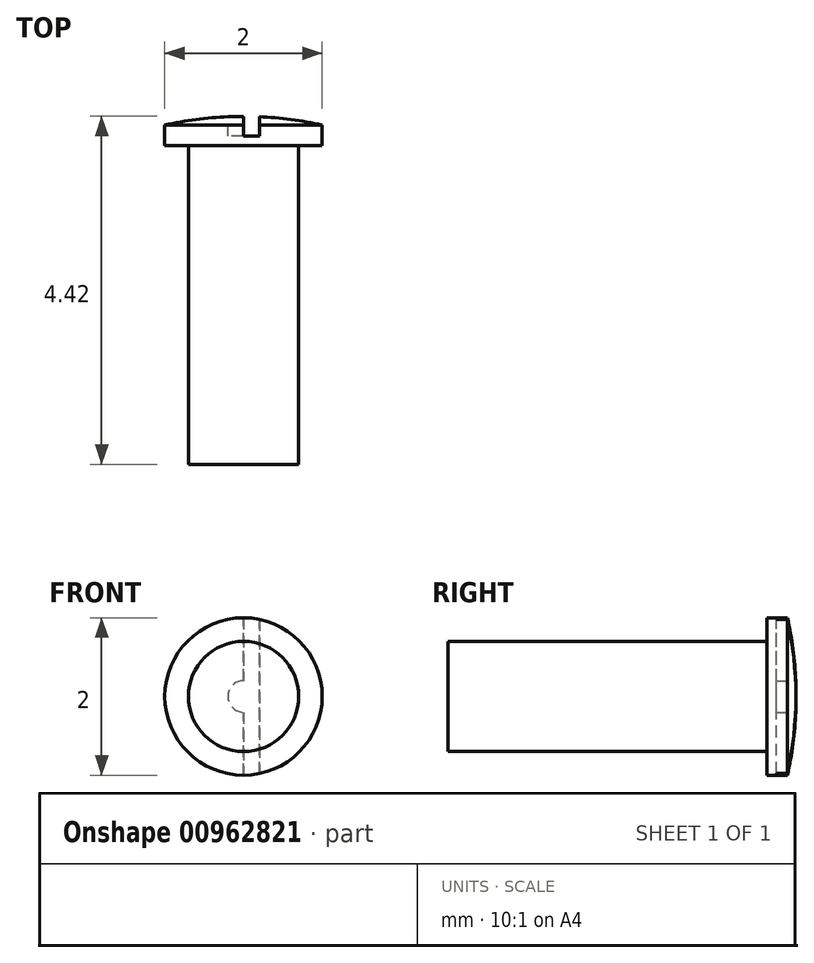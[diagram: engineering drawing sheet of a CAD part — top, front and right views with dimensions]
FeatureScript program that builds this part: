
annotation { "Feature Type Name" : "Feature", "Feature Type Description" : "" }
export const myFeature = defineFeature(function(context is Context, id is Id, definition is map)
    precondition{}
    {
        {
            var Q0;
            Q0=qCreatedBy(makeId("Top.planeOp"),FACE);
            var sketch = newSketch(context, id + "F0", { "sketchPlane" : qUnion([Q0])});
            skLineSegment(sketch, "E0", {"start": v(0, 0) * mm, "end": v(0.7, 0) * mm});
            skLineSegment(sketch, "E1", {"start": v(0.7, 0) * mm, "end": v(0.7, 4.05) * mm});
            skLineSegment(sketch, "E2", {"start": v(0.7, 4.05) * mm, "end": v(1, 4.05) * mm});
            skLineSegment(sketch, "E3", {"start": v(1, 4.05) * mm, "end": v(1, 4.3) * mm});
            skLineSegment(sketch, "E4", {"start": v(0, 4.42) * mm, "end": v(0, 0) * mm});
            skArc(sketch, "E5", {"start": v(1, 4.3) * mm, "mid": v(0.5, 4.4) * mm, "end": v(0, 4.42) * mm});
            skLineSegment(sketch, "E6", {"start": v(0, 4.42) * mm, "end": v(1, 4.42) * mm});
            skLineSegment(sketch, "E7", {"start": v(1, 4.42) * mm, "end": v(1, 4.3) * mm});
            skLineSegment(sketch, "E8.bottom", {"start": v(0, 4.42) * mm, "end": v(0.2, 4.42) * mm});
            skLineSegment(sketch, "E8.top", {"start": v(0, 4.17) * mm, "end": v(0.2, 4.17) * mm});
            skLineSegment(sketch, "E8.left", {"start": v(0, 4.42) * mm, "end": v(0, 4.17) * mm});
            skLineSegment(sketch, "E8.right", {"start": v(0.2, 4.42) * mm, "end": v(0.2, 4.17) * mm});
            skLineSegment(sketch, "E9.MirrorCS", {"start": v(0, 4.17) * mm, "end": v(-0.2, 4.17) * mm});
            skLineSegment(sketch, "E10.MirrorCS", {"start": v(-0.2, 4.42) * mm, "end": v(-0.2, 4.17) * mm});
            skLineSegment(sketch, "E11.MirrorCS", {"start": v(0, 4.42) * mm, "end": v(-0.2, 4.42) * mm});
            skSolve(sketch);
        }
        {
            var Q0;
            Q0=makeQuery(id+"F0.imprint","IMPRINT",FACE,{"disambiguationData":[TD([[makeQuery(id+"F0.imprint","IMPRINT",EDGE,{"derivedFrom":sQuery(id+"F0.wireOp",EDGE,"E0")}),1.0]])]});
            var Q1;
            Q1=sQuery(id+"F0.wireOp",EDGE,"E4");
            revolve(context, id + "F1", {"surfaceOperationType" : NewSurfaceOperationType.NEW, "entities" : qUnion([Q0]), "axis" : qUnion([Q1]), "revolveType" : RevolveType.FULL});
        }
        {
            var Q0;
            {var subQ4=sQuery(id+"F0.wireOp",EDGE,"E8.top");Q0=makeQuery(id+"F0.imprint","IMPRINT",FACE,{"disambiguationData":[TD([[makeQuery(id+"F0.imprint","IMPRINT",EDGE,{"derivedFrom":subQ4}),1.0]])]});}
            var Q1;
            Q1=makeQuery(id+"F0.imprint","IMPRINT",FACE,{"disambiguationData":[TD([[makeQuery(id+"F0.imprint","IMPRINT",EDGE,{"derivedFrom":sQuery(id+"F0.wireOp",EDGE,"E8.left")}),-1.0]])]});
            extrude(context, id + "F2", {"entities" : qUnion([Q0, Q1]), "operationType" : NewBodyOperationType.REMOVE, "endBound" : BoundingType.SYMMETRIC, "oppositeDirection" : true, "depth" : 25 * mm, "offsetDistance" : 25 * mm});
        }
    });
